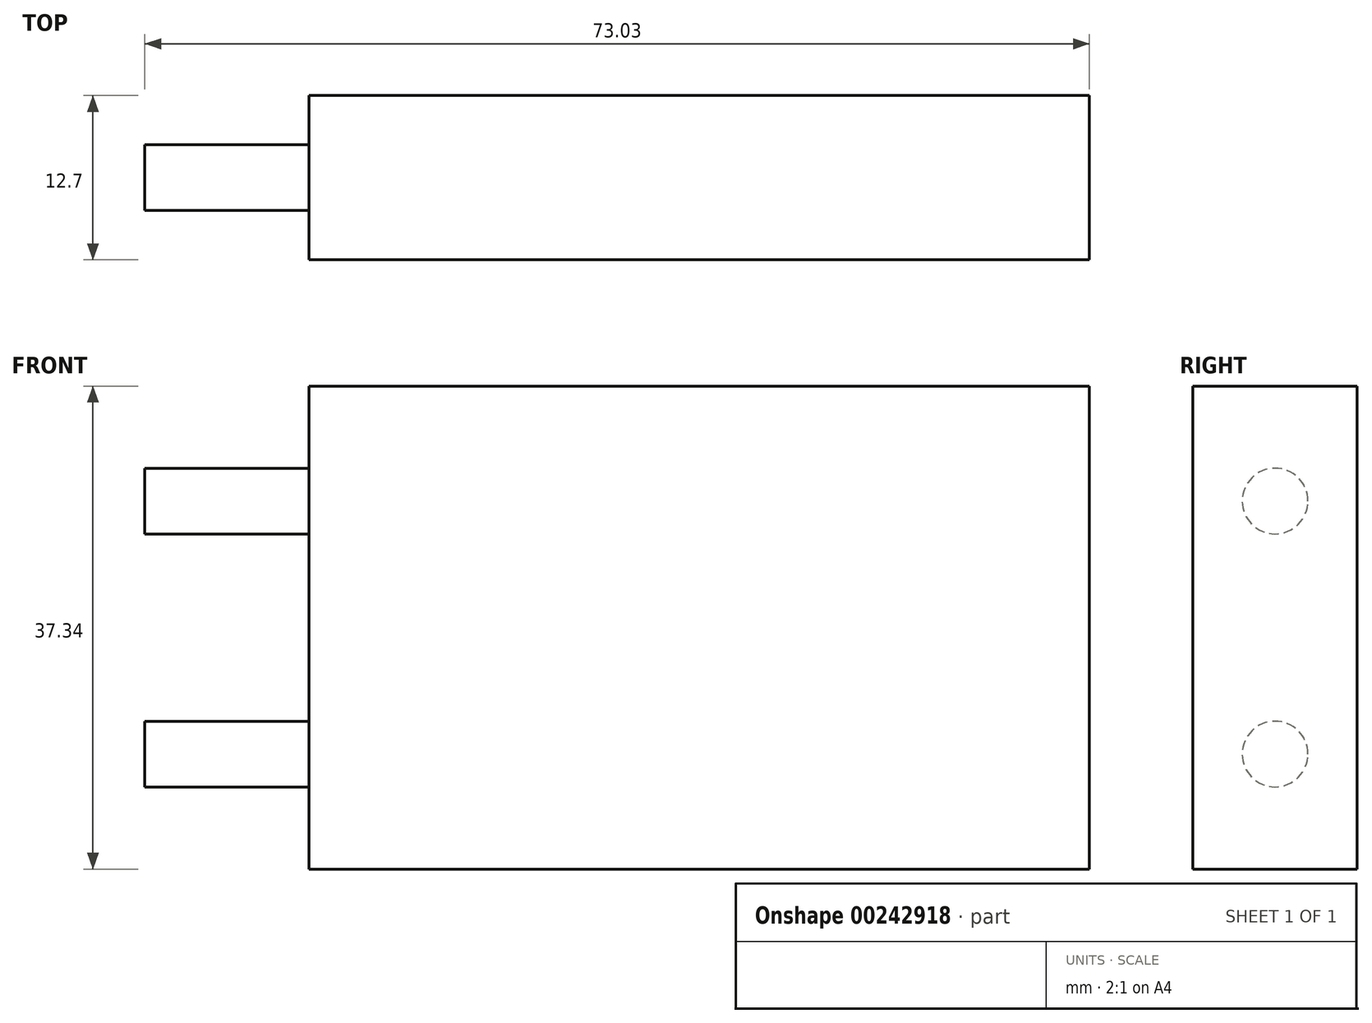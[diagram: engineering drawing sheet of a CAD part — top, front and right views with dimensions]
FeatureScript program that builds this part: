
annotation { "Feature Type Name" : "Feature", "Feature Type Description" : "" }
export const myFeature = defineFeature(function(context is Context, id is Id, definition is map)
    precondition{}
    {
        {
            var Q0;
            Q0=qCreatedBy(makeId("Front.planeOp"),FACE);
            var sketch = newSketch(context, id + "F0", { "sketchPlane" : qUnion([Q0])});
            skLineSegment(sketch, "E0", {"start": v(0, 0) * mm, "end": v(0, 38.1) * mm});
            skLineSegment(sketch, "E1", {"start": v(0, 38.1) * mm, "end": v(60.33, 38.1) * mm});
            skLineSegment(sketch, "E2", {"start": v(60.33, 38.1) * mm, "end": v(60.33, 0) * mm});
            skLineSegment(sketch, "E3", {"start": v(60.33, 0) * mm, "end": v(0, 0) * mm});
            skSolve(sketch);
        }
        {
            var Q0;
            Q0=makeQuery(id+"F0.imprint","IMPRINT",FACE,{"disambiguationData":[TD([[makeQuery(id+"F0.imprint","IMPRINT",EDGE,{"derivedFrom":sQuery(id+"F0.wireOp",EDGE,"E0")}),-1.0]])]});
            extrude(context, id + "F1", {"entities" : qUnion([Q0]), "depth" : 12.7 * mm});
        }
        {
            var Q0;
            Q0=makeQuery(id+"F1.opExtrude","SWEPT_FACE",FACE,{"disambiguationData":[OSD([sQuery(id+"F0.wireOp",EDGE,"E1")])]});
            var sketch = newSketch(context, id + "F2", { "sketchPlane" : qUnion([Q0])});
            skLineSegment(sketch, "E4.bottom", {"start": v(0, 0) * mm, "end": v(-7.62, 0) * mm});
            skLineSegment(sketch, "E4.top", {"start": v(0, -12.7) * mm, "end": v(-7.62, -12.7) * mm});
            skLineSegment(sketch, "E4.left", {"start": v(0, 0) * mm, "end": v(0, -12.7) * mm});
            skLineSegment(sketch, "E4.right", {"start": v(-7.62, 0) * mm, "end": v(-7.62, -12.7) * mm});
            skLineSegment(sketch, "E5", {"start": v(-7.62, -12.7) * mm, "end": v(0, -9.93) * mm});
            skLineSegment(sketch, "E6", {"start": v(0, -9.93) * mm, "end": v(0, -2.77) * mm});
            skLineSegment(sketch, "E7", {"start": v(0, -2.77) * mm, "end": v(-7.62, 0) * mm});
            skSolve(sketch);
        }
        {
            var Q0;
            Q0=makeQuery(id+"F2.imprint","IMPRINT",FACE,{"disambiguationData":[TD([[makeQuery(id+"F2.imprint","IMPRINT",EDGE,{"derivedFrom":sQuery(id+"F2.wireOp",EDGE,"E4.right")}),1.0]])]});
            extrude(context, id + "F3", {"entities" : qUnion([Q0]), "operationType" : NewBodyOperationType.ADD, "oppositeDirection" : true, "depth" : 38.1 * mm});
        }
        {
            var Q0;
            Q0=makeQuery(id+"F3.boolean.opBoolean","MERGE",FACE,{"derivedFrom":[makeQuery(id+"F1.opExtrude","SWEPT_FACE",FACE,{"disambiguationData":[OSD([sQuery(id+"F0.wireOp",EDGE,"E3")])]}),makeQuery(id+"F3.opExtrude","CAP_FACE",FACE,{"disambiguationData":[OSD([sQuery(id+"F2.wireOp",EDGE,"E4.right"),sQuery(id+"F2.wireOp",EDGE,"E5"),sQuery(id+"F2.wireOp",EDGE,"E6"),sQuery(id+"F2.wireOp",EDGE,"E7")])],"isStart":false})]});
            var sketch = newSketch(context, id + "F4", { "sketchPlane" : qUnion([Q0])});
            skLineSegment(sketch, "E8.bottom", {"start": v(0, 0) * mm, "end": v(-11.26, 0) * mm});
            skLineSegment(sketch, "E8.top", {"start": v(0, 14.84) * mm, "end": v(-11.26, 14.84) * mm});
            skLineSegment(sketch, "E8.left", {"start": v(0, 0) * mm, "end": v(0, 14.84) * mm});
            skLineSegment(sketch, "E8.right", {"start": v(-11.26, 0) * mm, "end": v(-11.26, 14.84) * mm});
            skSolve(sketch);
        }
        {
            var Q0;
            Q0=qSketchRegion(id+"F4",true);
            extrude(context, id + "F5", {"entities" : qUnion([Q0]), "operationType" : NewBodyOperationType.REMOVE, "oppositeDirection" : true, "depth" : 3.17 * mm});
        }
        {
            var Q0;
            Q0=makeQuery(id+"F1.opExtrude","SWEPT_FACE",FACE,{"disambiguationData":[OSD([sQuery(id+"F0.wireOp",EDGE,"E2")])]});
            var sketch = newSketch(context, id + "F6", { "sketchPlane" : qUnion([Q0])});
            skLineSegment(sketch, "E9.bottom", {"start": v(0, 38.1) * mm, "end": v(-12.7, 38.1) * mm});
            skLineSegment(sketch, "E9.top", {"start": v(0, 37.85) * mm, "end": v(-12.7, 37.85) * mm});
            skLineSegment(sketch, "E9.left", {"start": v(0, 38.1) * mm, "end": v(0, 37.85) * mm});
            skLineSegment(sketch, "E9.right", {"start": v(-12.7, 38.1) * mm, "end": v(-12.7, 37.85) * mm});
            skSolve(sketch);
        }
        {
            var Q0;
            Q0=makeQuery(id+"F6.imprint","IMPRINT",FACE,{"disambiguationData":[TD([[makeQuery(id+"F6.imprint","IMPRINT",EDGE,{"derivedFrom":sQuery(id+"F6.wireOp",EDGE,"E9.bottom")}),-1.0]])]});
            extrude(context, id + "F7", {"entities" : qUnion([Q0]), "operationType" : NewBodyOperationType.REMOVE, "oppositeDirection" : true, "depth" : 101.6 * mm});
        }
        {
            var Q0;
            Q0=makeQuery(id+"F5.boolean.opBoolean","COPY",FACE,{"derivedFrom":makeQuery(id+"F5.opExtrude","CAP_FACE",FACE,{"disambiguationData":[OSD([sQuery(id+"F4.wireOp",EDGE,"E8.bottom"),sQuery(id+"F4.wireOp",EDGE,"E8.top"),sQuery(id+"F4.wireOp",EDGE,"E8.left"),sQuery(id+"F4.wireOp",EDGE,"E8.right")])],"isStart":false})});
            var sketch = newSketch(context, id + "F8", { "sketchPlane" : qUnion([Q0])});
            skLineSegment(sketch, "E10", {"start": v(0, 2.77) * mm, "end": v(-7.62, 2.77) * mm});
            skLineSegment(sketch, "E11", {"start": v(-7.62, 2.77) * mm, "end": v(-7.62, 0) * mm});
            skLineSegment(sketch, "E12", {"start": v(-7.62, 0) * mm, "end": v(0, 2.77) * mm});
            skLineSegment(sketch, "E13", {"start": v(0, 3.43) * mm, "end": v(-7.62, 3.43) * mm});
            skLineSegment(sketch, "E14", {"start": v(-7.62, 3.43) * mm, "end": v(-7.62, 2.77) * mm});
            skSolve(sketch);
        }
        {
            var Q0;
            {var subQ0=sQuery(id+"F2.wireOp",EDGE,"E7");var subQ2=sQuery(id+"F2.wireOp",EDGE,"E5");var subQ10=sQuery(id+"F0.wireOp",EDGE,"E0");var subQ12=makeQuery(id+"F1.opExtrude","SWEPT_FACE",FACE,{"disambiguationData":[OSD([subQ10])]});Q0=makeQuery(id+"F5.boolean.opBoolean","MERGE",FACE,{"derivedFrom":[makeQuery(id+"F3.boolean.opBoolean","SPLIT",FACE,{"disambiguationData":[TD([makeQuery(id+"F3.opExtrude","SWEPT_FACE",FACE,{"disambiguationData":[OSD([subQ0])]})])],"derivedFrom":subQ12}),makeQuery(id+"F3.boolean.opBoolean","SPLIT",FACE,{"disambiguationData":[TD([makeQuery(id+"F3.opExtrude","SWEPT_FACE",FACE,{"disambiguationData":[OSD([subQ2])]})])],"derivedFrom":subQ12}),makeQuery(id+"F5.opExtrude","SWEPT_FACE",FACE,{"disambiguationData":[OSD([sQuery(id+"F4.wireOp",EDGE,"E8.left")])]})]});}
            var sketch = newSketch(context, id + "F9", { "sketchPlane" : qUnion([Q0])});
            skLineSegment(sketch, "E15", {"start": v(2.77, 3.18) * mm, "end": v(2.77, 0) * mm});
            skLineSegment(sketch, "E16", {"start": v(2.77, 0) * mm, "end": v(9.93, 0) * mm});
            skLineSegment(sketch, "E17", {"start": v(9.93, 0) * mm, "end": v(9.93, 3.17) * mm});
            skSolve(sketch);
        }
        {
            var Q0;
            {var subQ0=sQuery(id+"F8.wireOp",EDGE,"E10");Q0=makeQuery(id+"F8.imprint","IMPRINT",FACE,{"disambiguationData":[TD([[makeQuery(id+"F8.imprint","IMPRINT",EDGE,{"derivedFrom":subQ0}),-1.0]])]});}
            var Q1;
            Q1=makeQuery(id+"F8.imprint","IMPRINT",FACE,{"disambiguationData":[TD([[makeQuery(id+"F8.imprint","IMPRINT",EDGE,{"derivedFrom":sQuery(id+"F8.wireOp",EDGE,"E10")}),1.0]])]});
            var Q2;
            Q2=sQuery(id+"F9.wireOp",EDGE,"E15");
            var Q3;
            Q3=sQuery(id+"F9.wireOp",EDGE,"E16");
            var Q4;
            Q4=sQuery(id+"F9.wireOp",EDGE,"E17");
            sweep(context, id + "F10", {"operationType" : NewBodyOperationType.ADD, "profiles" : qUnion([Q0, Q1]), "path" : qUnion([Q2, Q3, Q4])});
        }
        {
            var Q0;
            Q0=makeQuery(id+"F10.boolean.opBoolean","MERGE",FACE,{"derivedFrom":[makeQuery(id+"F3.opExtrude","SWEPT_FACE",FACE,{"disambiguationData":[OSD([sQuery(id+"F2.wireOp",EDGE,"E4.right")])]}),makeQuery(id+"F10.opSweep","SWEPT_FACE",FACE,{"disambiguationData":[OSD([sQuery(id+"F8.wireOp",EDGE,"E11"),sQuery(id+"F8.wireOp",EDGE,"E14"),sQuery(id+"F9.wireOp",EDGE,"E15")])]})]});
            var sketch = newSketch(context, id + "F11", { "sketchPlane" : qUnion([Q0])});
            skLineSegment(sketch, "E18.bottom", {"start": v(3.43, 3.18) * mm, "end": v(9.27, 3.18) * mm});
            skLineSegment(sketch, "E18.top", {"start": v(3.43, 0.66) * mm, "end": v(9.27, 0.66) * mm});
            skLineSegment(sketch, "E18.left", {"start": v(3.43, 3.18) * mm, "end": v(3.43, 0.66) * mm});
            skLineSegment(sketch, "E18.right", {"start": v(9.27, 3.18) * mm, "end": v(9.27, 0.66) * mm});
            skSolve(sketch);
        }
        {
            var Q0;
            Q0=qSketchRegion(id+"F11",true);
            extrude(context, id + "F12", {"entities" : qUnion([Q0]), "operationType" : NewBodyOperationType.ADD, "oppositeDirection" : true, "depth" : 7.62 * mm});
        }
        {
            var Q0;
            Q0=makeQuery(id+"F1.opExtrude","SWEPT_FACE",FACE,{"disambiguationData":[OSD([sQuery(id+"F0.wireOp",EDGE,"E2")])]});
            var sketch = newSketch(context, id + "F13", { "sketchPlane" : qUnion([Q0])});
            skLineSegment(sketch, "E19.bottom", {"start": v(0, 37.85) * mm, "end": v(-12.7, 37.85) * mm});
            skLineSegment(sketch, "E19.top", {"start": v(0, 37.34) * mm, "end": v(-12.7, 37.34) * mm});
            skLineSegment(sketch, "E19.left", {"start": v(0, 37.85) * mm, "end": v(0, 37.34) * mm});
            skLineSegment(sketch, "E19.right", {"start": v(-12.7, 37.85) * mm, "end": v(-12.7, 37.34) * mm});
            skSolve(sketch);
        }
        {
            var Q0;
            Q0=makeQuery(id+"F13.imprint","IMPRINT",FACE,{"disambiguationData":[TD([[makeQuery(id+"F13.imprint","IMPRINT",EDGE,{"derivedFrom":sQuery(id+"F13.wireOp",EDGE,"E19.bottom")}),1.0]])]});
            extrude(context, id + "F14", {"entities" : qUnion([Q0]), "operationType" : NewBodyOperationType.REMOVE, "oppositeDirection" : true, "depth" : 101.6 * mm});
        }
        {
            var Q0;
            Q0=makeQuery(id+"F14.boolean.opBoolean","COPY",FACE,{"derivedFrom":makeQuery(id+"F14.opExtrude","SWEPT_FACE",FACE,{"disambiguationData":[OSD([sQuery(id+"F13.wireOp",EDGE,"E19.top")])]})});
            var sketch = newSketch(context, id + "F15", { "sketchPlane" : qUnion([Q0])});
            skLineSegment(sketch, "E20", {"start": v(-7.62, 0) * mm, "end": v(-7.62, -12.7) * mm});
            skLineSegment(sketch, "E21", {"start": v(-7.62, -12.7) * mm, "end": v(0, -9.93) * mm});
            skLineSegment(sketch, "E22", {"start": v(0, -9.93) * mm, "end": v(0, -2.77) * mm});
            skLineSegment(sketch, "E23", {"start": v(0, -2.77) * mm, "end": v(-7.62, 0) * mm});
            skSolve(sketch);
        }
        {
            var Q0;
            Q0=makeQuery(id+"F15.imprint","IMPRINT",FACE,{"disambiguationData":[TD([[makeQuery(id+"F15.imprint","IMPRINT",EDGE,{"derivedFrom":sQuery(id+"F15.wireOp",EDGE,"E20")}),-1.0]])]});
            extrude(context, id + "F16", {"entities" : qUnion([Q0]), "operationType" : NewBodyOperationType.REMOVE, "oppositeDirection" : true, "depth" : 17.78 * mm});
        }
        {
            var Q0;
            Q0=makeQuery(id+"F16.boolean.opBoolean","COPY",FACE,{"derivedFrom":makeQuery(id+"F16.opExtrude","CAP_FACE",FACE,{"disambiguationData":[OSD([sQuery(id+"F15.wireOp",EDGE,"E20"),sQuery(id+"F15.wireOp",EDGE,"E21"),sQuery(id+"F15.wireOp",EDGE,"E22"),sQuery(id+"F15.wireOp",EDGE,"E23")])],"isStart":false})});
            var sketch = newSketch(context, id + "F17", { "sketchPlane" : qUnion([Q0])});
            skLineSegment(sketch, "E24", {"start": v(-7.62, -12.7) * mm, "end": v(0, -9.93) * mm});
            skLineSegment(sketch, "E25", {"start": v(0, -9.93) * mm, "end": v(0, -2.77) * mm});
            skLineSegment(sketch, "E26", {"start": v(0, -2.77) * mm, "end": v(-7.62, 0) * mm});
            skLineSegment(sketch, "E27", {"start": v(-7.62, 0) * mm, "end": v(-7.62, -12.7) * mm});
            skSolve(sketch);
        }
        {
            var Q0;
            Q0=makeQuery(id+"F17.imprint","IMPRINT",FACE,{"disambiguationData":[TD([[makeQuery(id+"F17.imprint","IMPRINT",EDGE,{"derivedFrom":sQuery(id+"F17.wireOp",EDGE,"E24")}),-1.0]])]});
            extrude(context, id + "F18", {"entities" : qUnion([Q0]), "operationType" : NewBodyOperationType.REMOVE, "oppositeDirection" : true, "depth" : 25.4 * mm});
        }
        {
            var Q0;
            {var subQ0=sQuery(id+"F2.wireOp",EDGE,"E5");var subQ1=makeQuery(id+"F3.opExtrude","SWEPT_FACE",FACE,{"disambiguationData":[OSD([subQ0])]});var subQ3=sQuery(id+"F2.wireOp",EDGE,"E7");var subQ11=sQuery(id+"F0.wireOp",EDGE,"E0");var subQ17=makeQuery(id+"F1.opExtrude","SWEPT_FACE",FACE,{"disambiguationData":[OSD([subQ11])]});var subQ19=makeQuery(id+"F3.opExtrude","SWEPT_FACE",FACE,{"disambiguationData":[OSD([subQ3])]});var subQ20=makeQuery(id+"F5.boolean.opBoolean","MERGE",FACE,{"derivedFrom":[makeQuery(id+"F3.boolean.opBoolean","SPLIT",FACE,{"disambiguationData":[TD([subQ19])],"derivedFrom":subQ17}),makeQuery(id+"F3.boolean.opBoolean","SPLIT",FACE,{"disambiguationData":[TD([subQ1])],"derivedFrom":subQ17}),makeQuery(id+"F5.opExtrude","SWEPT_FACE",FACE,{"disambiguationData":[OSD([sQuery(id+"F4.wireOp",EDGE,"E8.left")])]})]});Q0=makeQuery(id+"F18.boolean.opBoolean","MERGE",FACE,{"derivedFrom":[makeQuery(id+"F16.boolean.opBoolean","MERGE",FACE,{"derivedFrom":[makeQuery(id+"F10.boolean.opBoolean","SPLIT",FACE,{"disambiguationData":[TD([subQ19])],"derivedFrom":subQ20}),makeQuery(id+"F10.boolean.opBoolean","SPLIT",FACE,{"disambiguationData":[TD([subQ1])],"derivedFrom":subQ20}),makeQuery(id+"F16.opExtrude","SWEPT_FACE",FACE,{"disambiguationData":[OSD([sQuery(id+"F15.wireOp",EDGE,"E22")])]})]}),makeQuery(id+"F18.opExtrude","SWEPT_FACE",FACE,{"disambiguationData":[OSD([sQuery(id+"F17.wireOp",EDGE,"E25")])]})]});}
            var sketch = newSketch(context, id + "F19", { "sketchPlane" : qUnion([Q0])});
            skLineSegment(sketch, "E28", {"start": v(0, 0) * mm, "end": v(0, 37.34) * mm});
            skLineSegment(sketch, "E29", {"start": v(6.35, 37.34) * mm, "end": v(6.35, 28.45) * mm});
            skLineSegment(sketch, "E30", {"start": v(6.35, 0) * mm, "end": v(6.35, 8.9) * mm});
            skCircle(sketch, "E31", {"center": v(6.35, 8.9) * mm, "radius": 2.54 * mm});
            skCircle(sketch, "E32", {"center": v(6.35, 28.45) * mm, "radius": 2.54 * mm});
            skSolve(sketch);
        }
        {
            var Q0;
            Q0=makeQuery(id+"F19.imprint","IMPRINT",FACE,{"disambiguationData":[TD([[makeQuery(id+"F19.imprint","IMPRINT",EDGE,{"derivedFrom":sQuery(id+"F19.wireOp",EDGE,"E31")}),1.0]])]});
            var Q1;
            Q1=makeQuery(id+"F19.imprint","IMPRINT",FACE,{"disambiguationData":[TD([[makeQuery(id+"F19.imprint","IMPRINT",EDGE,{"derivedFrom":sQuery(id+"F19.wireOp",EDGE,"E32")}),1.0]])]});
            extrude(context, id + "F20", {"entities" : qUnion([Q0, Q1]), "operationType" : NewBodyOperationType.ADD, "depth" : 12.7 * mm});
        }
    });
